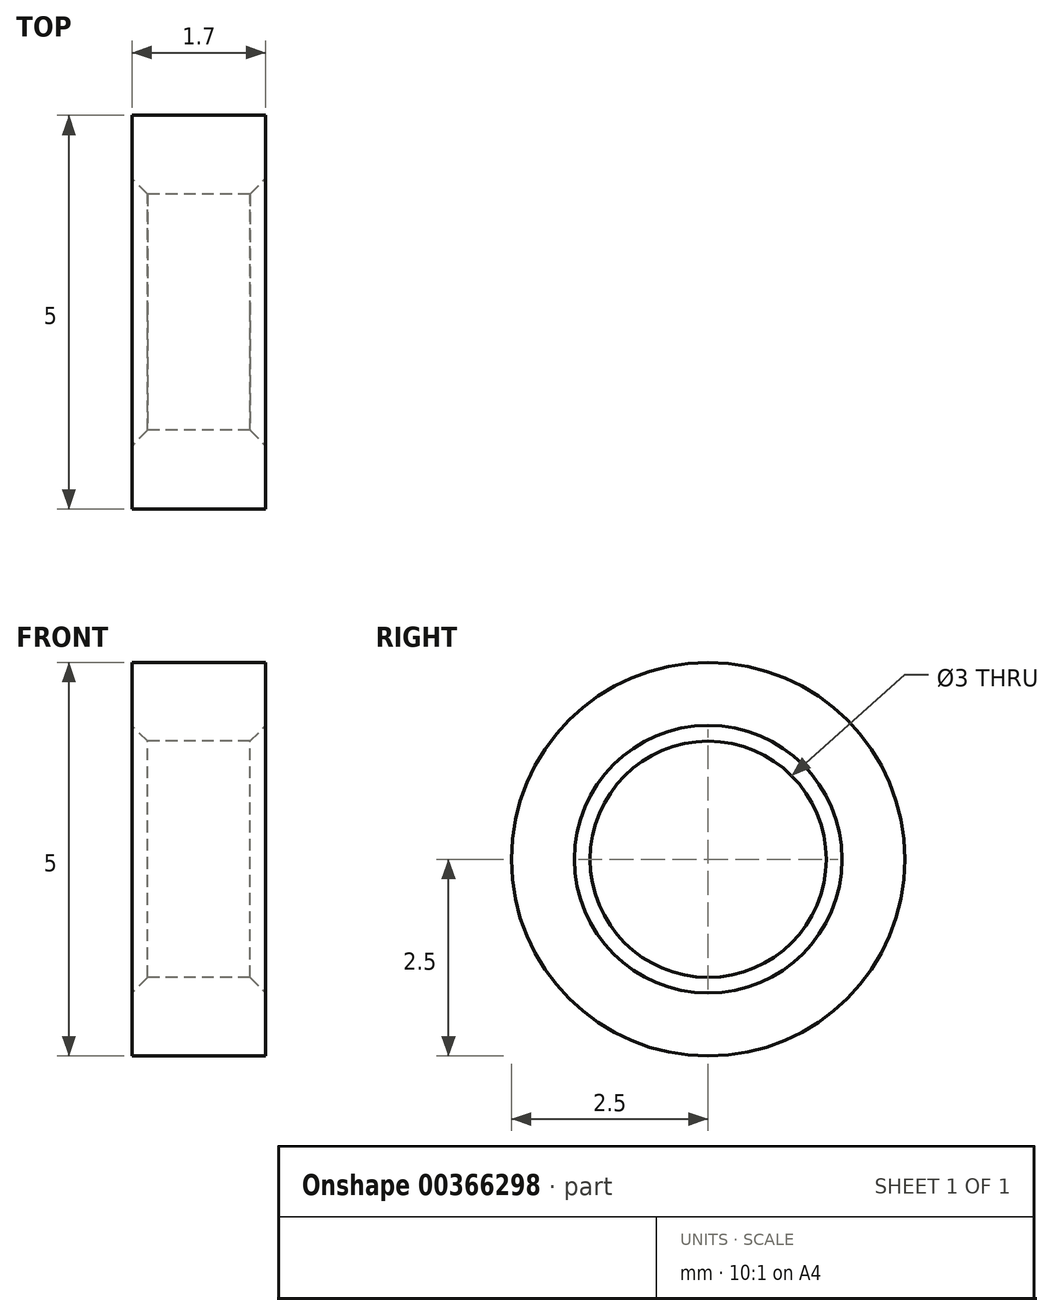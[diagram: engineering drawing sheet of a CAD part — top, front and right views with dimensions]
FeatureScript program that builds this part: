
annotation { "Feature Type Name" : "Feature", "Feature Type Description" : "" }
export const myFeature = defineFeature(function(context is Context, id is Id, definition is map)
    precondition{}
    {
        {
            var Q0;
            Q0=qCreatedBy(makeId("Right.planeOp"),FACE);
            var sketch = newSketch(context, id + "F0", { "sketchPlane" : qUnion([Q0])});
            skCircle(sketch, "E0", {"center": v(0, 0) * mm, "radius": 2.5 * mm});
            skCircle(sketch, "E1", {"center": v(0, 0) * mm, "radius": 1.5 * mm});
            skSolve(sketch);
        }
        {
            var Q0;
            Q0=makeQuery(id+"F0.imprint","IMPRINT",FACE,{"disambiguationData":[TD([[makeQuery(id+"F0.imprint","IMPRINT",EDGE,{"derivedFrom":sQuery(id+"F0.wireOp",EDGE,"E0")}),1.0]])]});
            extrude(context, id + "F1", {"entities" : qUnion([Q0]), "depth" : 1.7 * mm});
        }
        {
            var Q0;
            Q0=makeQuery(id+"F1.opExtrude","SWEPT_FACE",FACE,{"disambiguationData":[OSD([sQuery(id+"F0.wireOp",EDGE,"E1")])]});
            chamfer(context, id + "F2", {"entities" : qUnion([Q0]), "width" : 0.2 * mm, "tangentPropagation" : true});
        }
    });
